# Revit family: Haworth_Patterns_FloatingBracket
name_source: partatom
category: Furniture Systems
revit_build: Autodesk Revit 2018 (Build: 20170223_1515(x64)
units: mm (PartAtom-declared; Revit-internal decimal feet)

## family parameters
Always vertical = Yes
Cut with Voids When Loaded = No
OmniClass Number = 23.40.70.14.64.21
OmniClass Title = Systems Furniture
Part Type = Normal
Room Calculation Point = No
Round Connector Dimension = Use Diameter
Shared = No
Work Plane-Based = No

## types (2) — shared parameters
Actual Depth = 3 99/256"
Actual Mounting Height = 27 7/8"
Actual Width = 16 51/128"
Assembly Code = E2020200
Bracket Finish = Haworth _ Paint _ Metallic Champagne
Description = Haworth - Patterns Floating Bracket
Manufacturer = Haworth
Model = Haworth - Patterns Floating Bracket
Revision Number = 2
Size = Verify Final Dim. w/ Haworth
Sustainability Info = http://www.haworth.com
URL = https://www.haworth.com
URL - Product = https://www.haworth.com
Warranty = http://www.haworth.com

## per-type parameters (varying)
| type | 1.5 Gap | 2.5 Gap | Gap Length |
| Bracket - 1.5 Gap | Yes | No | 1 1/2" |
| Bracket - 2.5 Gap | No | Yes | 2 39/128" |

## geometry (parser evidence)
native form markers: Sweep x8
no freeform markers — native parametric forms only
